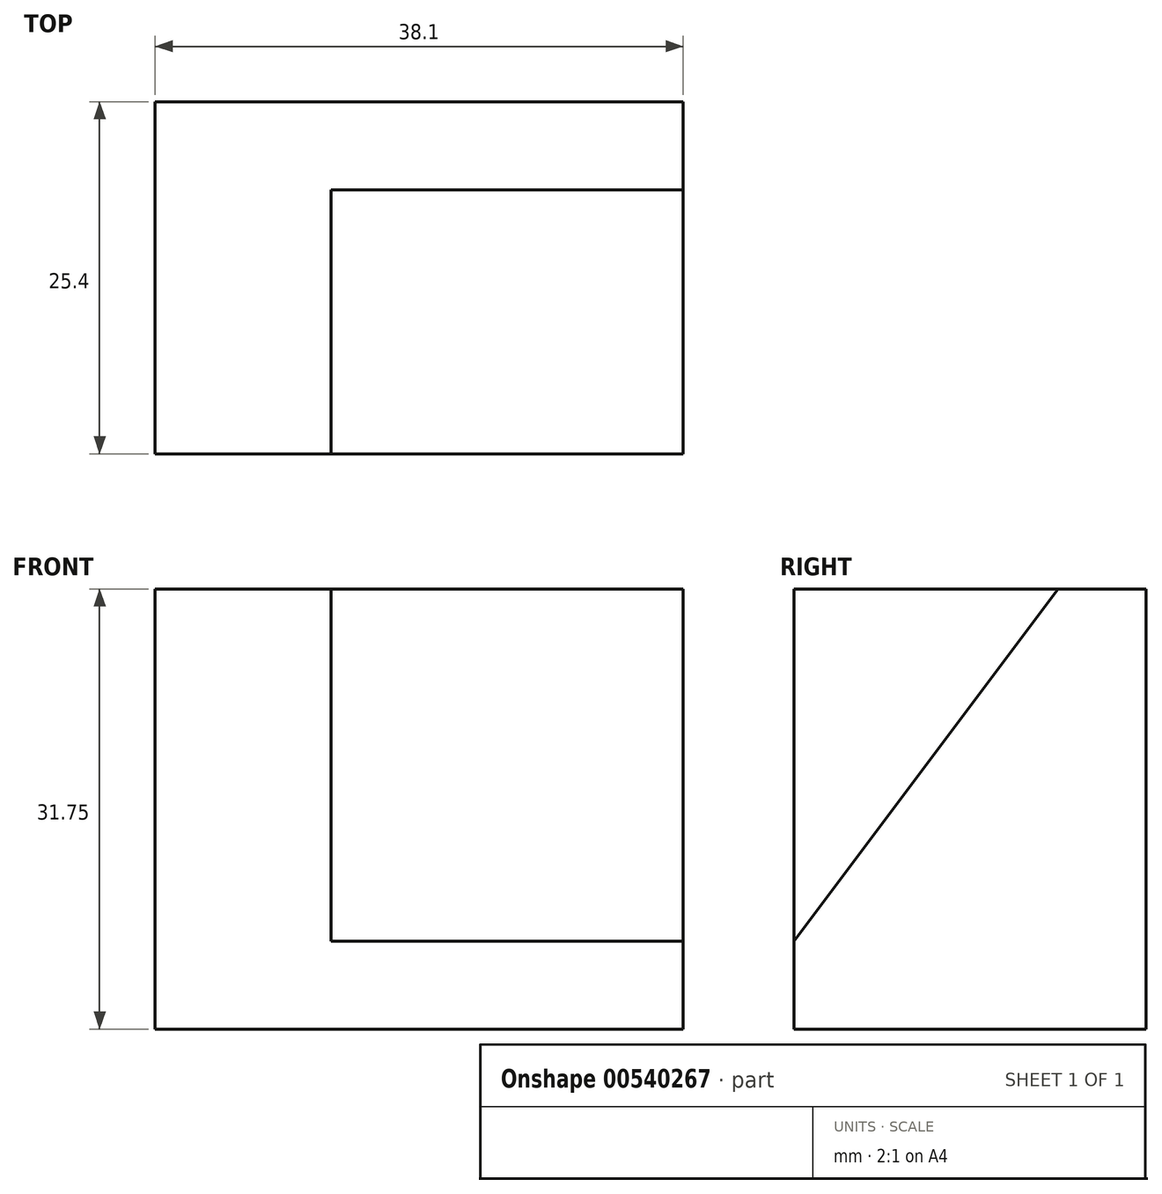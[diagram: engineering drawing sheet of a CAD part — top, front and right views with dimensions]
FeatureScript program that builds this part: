
annotation { "Feature Type Name" : "Feature", "Feature Type Description" : "" }
export const myFeature = defineFeature(function(context is Context, id is Id, definition is map)
    precondition{}
    {
        {
            var Q0;
            Q0=qCreatedBy(makeId("Front.planeOp"),FACE);
            var sketch = newSketch(context, id + "F0", { "sketchPlane" : qUnion([Q0])});
            skLineSegment(sketch, "E0", {"start": v(-65.7, 31.75) * mm, "end": v(-65.7, 0) * mm});
            skLineSegment(sketch, "E1", {"start": v(-65.7, 0) * mm, "end": v(-27.6, 0) * mm});
            skLineSegment(sketch, "E2", {"start": v(-27.6, 0) * mm, "end": v(-27.6, 31.75) * mm});
            skLineSegment(sketch, "E3", {"start": v(-27.6, 31.75) * mm, "end": v(-65.7, 31.75) * mm});
            skSolve(sketch);
        }
        {
            var Q0;
            Q0 = qSketchRegion(id + "F0", true);
            extrude(context, id + "F1", {"entities" : qUnion([Q0]), "depth" : 25.4 * mm, "offsetDistance" : 25.4 * mm});
        }
        {
            var Q0;
            Q0=makeQuery(id+"F1.opExtrude","SWEPT_FACE",FACE,{"disambiguationData":[OSD([sQuery(id+"F0.wireOp",EDGE,"E2")])]});
            var sketch = newSketch(context, id + "F2", { "sketchPlane" : qUnion([Q0])});
            skLineSegment(sketch, "E4", {"start": v(-6.35, 31.75) * mm, "end": v(-25.4, 6.35) * mm});
            skSolve(sketch);
        }
        {
            var Q0;
            Q0 = qSketchRegion(id + "F2", true);
            var Q1;
            {var subQ0=sQuery(id+"F2.wireOp",EDGE,"E4");Q1=makeQuery(id+"F2.imprint","IMPRINT",FACE,{"disambiguationData":[TD([[makeQuery(id+"F2.imprint","IMPRINT",EDGE,{"derivedFrom":subQ0}),-1.0]])]});}
            extrude(context, id + "F3", {"entities" : qUnion([Q0, Q1]), "operationType" : NewBodyOperationType.REMOVE, "oppositeDirection" : true, "depth" : 25.4 * mm, "offsetDistance" : 25.4 * mm});
        }
    });
